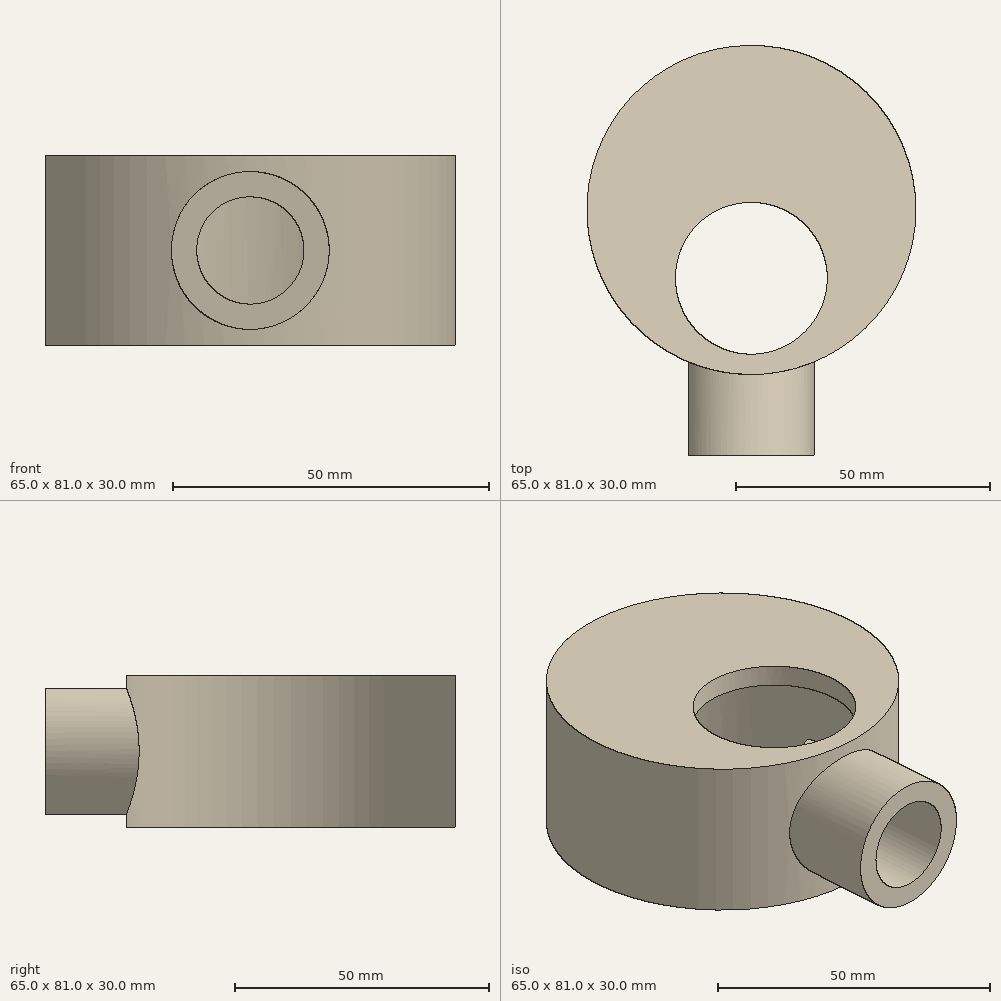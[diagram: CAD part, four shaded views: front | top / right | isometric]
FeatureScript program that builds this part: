
annotation { "Feature Type Name" : "Feature", "Feature Type Description" : "" }
export const myFeature = defineFeature(function(context is Context, id is Id, definition is map)
    precondition{}
    {
        {
            var Q0;
            Q0=qCreatedBy(makeId("Front.planeOp"),FACE);
            var sketch = newSketch(context, id + "F0", { "sketchPlane" : qUnion([Q0])});
            skLineSegment(sketch, "E0", {"start": v(0, 0) * mm, "end": v(0, 15) * mm, "construction": true});
            skCircle(sketch, "E1", {"center": v(0, 15) * mm, "radius": 12.5 * mm});
            skSolve(sketch);
        }
        {
            var Q0;
            Q0 = qSketchRegion(id + "F0", true);
            extrude(context, id + "F1", {"entities" : qUnion([Q0]), "endBound" : BoundingType.SYMMETRIC, "depth" : 40 * mm, "offsetDistance" : 25 * mm});
        }
        {
            var Q0;
            Q0=qCreatedBy(makeId("Top.planeOp"),FACE);
            var sketch = newSketch(context, id + "F2", { "sketchPlane" : qUnion([Q0])});
            skLineSegment(sketch, "E2", {"start": v(0, 0) * mm, "end": v(0, -4) * mm, "construction": true});
            skLineSegment(sketch, "E3", {"start": v(0, -4) * mm, "end": v(0, 61) * mm, "construction": true});
            skCircle(sketch, "E4", {"center": v(0, 28.5) * mm, "radius": 32.5 * mm});
            skSolve(sketch);
        }
        {
            var Q0;
            Q0 = qSketchRegion(id + "F2", true);
            extrude(context, id + "F3", {"entities" : qUnion([Q0]), "operationType" : NewBodyOperationType.ADD, "depth" : 30 * mm, "offsetDistance" : 25 * mm});
        }
        {
            var Q0;
            Q0=qCreatedBy(makeId("Top.planeOp"),FACE);
            var sketch = newSketch(context, id + "F4", { "sketchPlane" : qUnion([Q0])});
            skLineSegment(sketch, "E5", {"start": v(0, 0) * mm, "end": v(0, -4) * mm, "construction": true});
            skLineSegment(sketch, "E6", {"start": v(0, -4) * mm, "end": v(0, 61) * mm, "construction": true});
            skCircle(sketch, "E7", {"center": v(0, 28.5) * mm, "radius": 28.5 * mm});
            skSolve(sketch);
        }
        {
            var Q0;
            Q0 = qSketchRegion(id + "F4", true);
            extrude(context, id + "F5", {"entities" : qUnion([Q0]), "operationType" : NewBodyOperationType.REMOVE, "depth" : 26 * mm, "offsetDistance" : 25 * mm});
        }
        {
            var Q0;
            Q0=qCreatedBy(makeId("Front.planeOp"),FACE);
            var sketch = newSketch(context, id + "F6", { "sketchPlane" : qUnion([Q0])});
            skLineSegment(sketch, "E8", {"start": v(0, 0) * mm, "end": v(0, 15) * mm, "construction": true});
            skCircle(sketch, "E9", {"center": v(0, 15) * mm, "radius": 11 * mm});
            skSolve(sketch);
        }
        {
            var Q0;
            Q0 = qSketchRegion(id + "F6", true);
            extrude(context, id + "F7", {"entities" : qUnion([Q0]), "operationType" : NewBodyOperationType.REMOVE, "oppositeDirection" : true, "depth" : 19.5 * mm, "offsetDistance" : 25 * mm});
        }
        {
            var Q0;
            Q0=qCreatedBy(makeId("Top.planeOp"),FACE);
            var sketch = newSketch(context, id + "F8", { "sketchPlane" : qUnion([Q0])});
            skLineSegment(sketch, "E10", {"start": v(0, 0) * mm, "end": v(0, 15) * mm, "construction": true});
            skCircle(sketch, "E11", {"center": v(0, 15) * mm, "radius": 15 * mm});
            skSolve(sketch);
        }
        {
            var Q0;
            Q0 = qSketchRegion(id + "F8", true);
            extrude(context, id + "F9", {"entities" : qUnion([Q0]), "operationType" : NewBodyOperationType.REMOVE, "depth" : 44.3 * mm, "offsetDistance" : 25 * mm});
        }
        {
            var Q0;
            Q0=qCreatedBy(makeId("Front.planeOp"),FACE);
            var sketch = newSketch(context, id + "F10", { "sketchPlane" : qUnion([Q0])});
            skLineSegment(sketch, "E12", {"start": v(0, 0) * mm, "end": v(0, 15) * mm, "construction": true});
            skCircle(sketch, "E13", {"center": v(0, 15) * mm, "radius": 8.5 * mm});
            skSolve(sketch);
        }
        {
            var Q0;
            Q0 = qSketchRegion(id + "F10", true);
            extrude(context, id + "F11", {"entities" : qUnion([Q0]), "operationType" : NewBodyOperationType.REMOVE, "depth" : 41.2 * mm, "offsetDistance" : 25 * mm});
        }
        {
            var Q0;
            Q0=qCreatedBy(makeId("Top.planeOp"),FACE);
            var sketch = newSketch(context, id + "F12", { "sketchPlane" : qUnion([Q0])});
            skLineSegment(sketch, "E14", {"start": v(0, 0) * mm, "end": v(0, -4) * mm, "construction": true});
            skLineSegment(sketch, "E15", {"start": v(0, -4) * mm, "end": v(0, 61) * mm, "construction": true});
            skArc(sketch, "E16", {"start": v(29, 34.14) * mm, "mid": v(23.36, 28.5) * mm, "end": v(29, 22.86) * mm});
            skLineSegment(sketch, "E17", {"start": v(29, 28.5) * mm, "end": v(29, 22.86) * mm});
            skLineSegment(sketch, "E18", {"start": v(29, 28.5) * mm, "end": v(29, 34.14) * mm});
            skLineSegment(sketch, "E19", {"start": v(29, 28.5) * mm, "end": v(23.36, 28.5) * mm, "construction": true});
            skCircle(sketch, "E20", {"center": v(26.18, 28.5) * mm, "radius": 1.5 * mm});
            skArc(sketch, "E21.MirrorCS", {"start": v(-29, 34.14) * mm, "mid": v(-23.36, 28.5) * mm, "end": v(-29, 22.86) * mm});
            skLineSegment(sketch, "E22.MirrorCS", {"start": v(-29, 28.5) * mm, "end": v(-29, 22.86) * mm});
            skLineSegment(sketch, "E23.MirrorCS", {"start": v(-29, 28.5) * mm, "end": v(-29, 34.14) * mm});
            skCircle(sketch, "E24.MirrorC", {"center": v(-26.18, 28.5) * mm, "radius": 1.5 * mm});
            skSolve(sketch);
        }
        {
            var Q0;
            Q0 = qSketchRegion(id + "F12", true);
            extrude(context, id + "F13", {"entities" : qUnion([Q0]), "operationType" : NewBodyOperationType.ADD, "depth" : 4 * mm, "offsetDistance" : 25 * mm});
        }
    });
